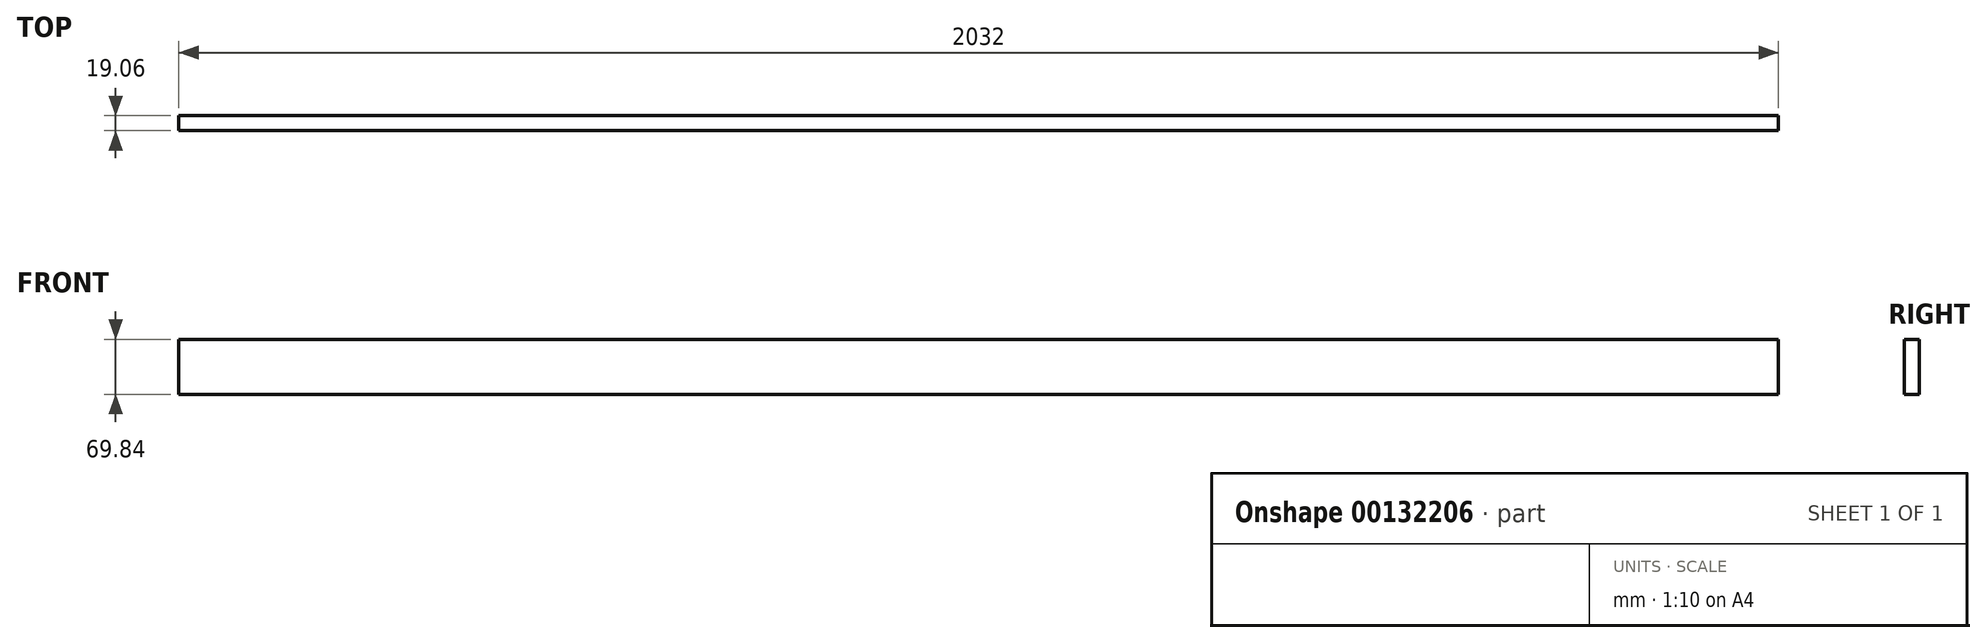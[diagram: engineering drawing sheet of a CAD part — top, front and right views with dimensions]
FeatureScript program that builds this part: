
annotation { "Feature Type Name" : "Feature", "Feature Type Description" : "" }
export const myFeature = defineFeature(function(context is Context, id is Id, definition is map)
    precondition{}
    {
        {
            var Q0;
            Q0=qCreatedBy(makeId("Front.planeOp"),FACE);
            var sketch = newSketch(context, id + "F0", { "sketchPlane" : qUnion([Q0])});
            skLineSegment(sketch, "E0.bottom", {"start": v(1016, 34.93) * mm, "end": v(-1016, 34.93) * mm});
            skLineSegment(sketch, "E0.top", {"start": v(1016, -34.93) * mm, "end": v(-1016, -34.93) * mm});
            skLineSegment(sketch, "E0.left", {"start": v(1016, 34.93) * mm, "end": v(1016, -34.93) * mm});
            skLineSegment(sketch, "E0.right", {"start": v(-1016, 34.93) * mm, "end": v(-1016, -34.93) * mm});
            skPoint(sketch, "E0.middle", {"position": v(0, 0) * mm});
            skSolve(sketch);
        }
        {
            var Q0;
            Q0=makeQuery(id+"F0.imprint","IMPRINT",FACE,{"disambiguationData":[TD([[makeQuery(id+"F0.imprint","IMPRINT",EDGE,{"derivedFrom":sQuery(id+"F0.wireOp",EDGE,"E0.bottom")}),1.0]])]});
            extrude(context, id + "F1", {"entities" : qUnion([Q0]), "endBound" : BoundingType.SYMMETRIC, "depth" : 19.05 * mm});
        }
    });
